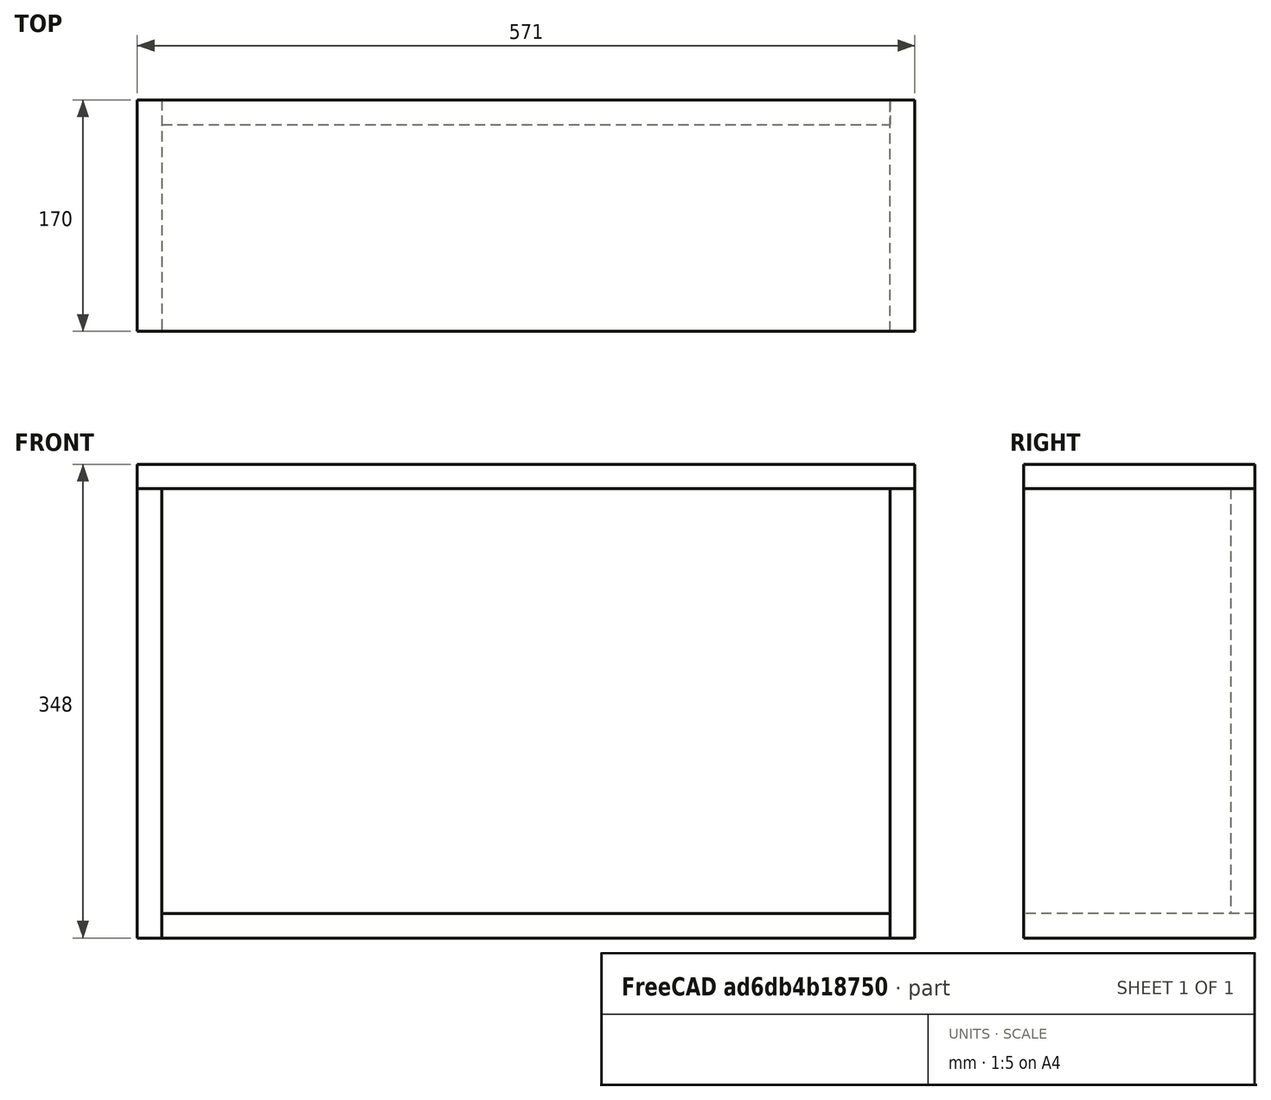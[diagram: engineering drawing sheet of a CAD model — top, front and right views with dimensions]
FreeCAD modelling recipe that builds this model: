
FCSTD DOCUMENT  (FreeCAD 0.17R13541 (Git))
Label: Case_2018-12-29
License: All rights reserved
LicenseURL: http://en.wikipedia.org/wiki/All_rights_reserved
objects: TechDraw::DrawViewDimension×10, Sketcher::SketchObject×5, PartDesign::Pad×5, PartDesign::Body×5, PartDesign::ShapeBinder×5, TechDraw::DrawViewPart×5, TechDraw::DrawSVGTemplate×1, TechDraw::DrawPage×1
note: 25 computed .brp shape members not serialized (recipe doc carries the construction recipe); baked Part::Feature solids carry a one-line shape summary decoded from their .brp

FEATURE [Sketcher::SketchObject] Sketch002
  MapMode = 5
  Placement = pos=(0,0,0) rot=(0.57735,0.57735,0.57735;2.0944rad)
  Support = -> [YZ_Plane002]
  sketch-geometry (4):
    g0: LineSegment StartX=-170 StartY=330 StartZ=0 EndX=0 EndY=330 EndZ=0
    g1: LineSegment StartX=0 StartY=330 StartZ=0 EndX=0 EndY=0 EndZ=0
    g2: LineSegment StartX=0 StartY=0 StartZ=0 EndX=-170 EndY=0 EndZ=0
    g3: LineSegment StartX=-170 StartY=0 StartZ=0 EndX=-170 EndY=330 EndZ=0
  constraints (11):
    c: Coincident(g0,g1)
    c: Coincident(g1,g2)
    c: Coincident(g2,g3)
    c: Coincident(g3,g0)
    c: Horizontal(g0)
    c: Horizontal(g2)
    c: Vertical(g1)
    c: Vertical(g3)
    c: DistanceX(g2,g2) = 170
    c: DistanceY(g3,g3) = 330
    c: Coincident(g-1,g1)
FEATURE [PartDesign::Pad] Pad002
  Length = 18
  Length2 = 100
  Placement = pos=(0,0,0) rot=(0.57735,0.57735,0.57735;2.0944rad)
  Profile = -> Sketch002
  Reversed = true
  Type = 0
FEATURE [PartDesign::Body] Body002  label="RightPlate"
  Group = -> [Sketch002,Pad002]
  Origin = -> Origin002
  Tip = -> Pad002
FEATURE [PartDesign::ShapeBinder] ShapeBinder
  Placement = pos=(-18,0,0) rot=(0,0,1;0rad)
  Support = -> [Pad002]
FEATURE [Sketcher::SketchObject] Sketch001
  ExternalGeometry = -> [ShapeBinder]
  MapMode = 5
  Support = -> [XY_Plane001]
  sketch-geometry (4):
    g0: LineSegment StartX=-553 StartY=0 StartZ=0 EndX=-18 EndY=0 EndZ=0
    g1: LineSegment StartX=-18 StartY=0 StartZ=0 EndX=-18 EndY=-170 EndZ=0
    g2: LineSegment StartX=-18 StartY=-170 StartZ=0 EndX=-553 EndY=-170 EndZ=0
    g3: LineSegment StartX=-553 StartY=-170 StartZ=0 EndX=-553 EndY=0 EndZ=0
  constraints (11):
    c: Coincident(g0,g1)
    c: Coincident(g1,g2)
    c: Coincident(g2,g3)
    c: Coincident(g3,g0)
    c: Horizontal(g0)
    c: Horizontal(g2)
    c: Vertical(g1)
    c: Vertical(g3)
    c: DistanceY(g1,g1) = 170
    c: DistanceX(g0,g0) = 535
    c: Coincident(g0,g-3)
FEATURE [PartDesign::Pad] Pad001
  Length = 18
  Length2 = 100
  Profile = -> Sketch001
  Type = 0
FEATURE [PartDesign::Body] Body001  label="BottomPlate"
  Group = -> [Sketch001,Pad001,ShapeBinder]
  Origin = -> Origin001
  Tip = -> Pad001
FEATURE [PartDesign::ShapeBinder] ShapeBinder001
  Placement = pos=(0,0,18) rot=(0,0,1;0rad)
  Support = -> [Pad001]
FEATURE [Sketcher::SketchObject] Sketch
  ExternalGeometry = -> [ShapeBinder001]
  MapMode = 5
  Placement = pos=(0,0,0) rot=(1,0,0;1.5708rad)
  Support = -> [XZ_Plane]
  sketch-geometry (4):
    g0: LineSegment StartX=-553 StartY=330 StartZ=0 EndX=-18 EndY=330 EndZ=0
    g1: LineSegment StartX=-18 StartY=330 StartZ=0 EndX=-18 EndY=18 EndZ=0
    g2: LineSegment StartX=-18 StartY=18 StartZ=0 EndX=-553 EndY=18 EndZ=0
    g3: LineSegment StartX=-553 StartY=18 StartZ=0 EndX=-553 EndY=330 EndZ=0
  constraints (11):
    c: Coincident(g0,g1)
    c: Coincident(g1,g2)
    c: Coincident(g2,g3)
    c: Coincident(g3,g0)
    c: Horizontal(g0)
    c: Horizontal(g2)
    c: Vertical(g1)
    c: Vertical(g3)
    c: DistanceX(g2,g2) = 535
    c: DistanceY(g1,g1) = 312
    c: Coincident(g1,g-3)
FEATURE [PartDesign::Pad] Pad
  Length = 18
  Length2 = 100
  Placement = pos=(0,0,0) rot=(1,0,0;1.5708rad)
  Profile = -> Sketch
  Type = 0
FEATURE [PartDesign::Body] Body  label="BackPlate"
  Group = -> [Sketch,Pad,ShapeBinder001]
  Origin = -> Origin
  Tip = -> Pad
FEATURE [PartDesign::ShapeBinder] ShapeBinder002
  Support = -> [Pad001]
FEATURE [Sketcher::SketchObject] Sketch003
  MapMode = 5
  Placement = pos=(-553,0,0) rot=(0.57735,-0.57735,-0.57735;2.0944rad)
  Support = -> [ShapeBinder002]
  sketch-geometry (4):
    g0: LineSegment StartX=0 StartY=330 StartZ=0 EndX=170 EndY=330 EndZ=0
    g1: LineSegment StartX=170 StartY=330 StartZ=0 EndX=170 EndY=0 EndZ=0
    g2: LineSegment StartX=170 StartY=0 StartZ=0 EndX=0 EndY=0 EndZ=0
    g3: LineSegment StartX=0 StartY=0 StartZ=0 EndX=0 EndY=330 EndZ=0
  constraints (11):
    c: Coincident(g0,g1)
    c: Coincident(g1,g2)
    c: Coincident(g2,g3)
    c: Coincident(g3,g0)
    c: Horizontal(g0)
    c: Horizontal(g2)
    c: Vertical(g1)
    c: Vertical(g3)
    c: DistanceX(g2,g2) = 170
    c: DistanceY(g3,g3) = 330
    c: Coincident(g-1,g2)
FEATURE [PartDesign::Pad] Pad003
  Length = 18
  Length2 = 100
  Profile = -> Sketch003
  Type = 0
FEATURE [PartDesign::Body] Body003  label="LeftPlate"
  Group = -> [ShapeBinder002,Sketch003,Pad003]
  Origin = -> Origin003
  Tip = -> Pad003
FEATURE [PartDesign::ShapeBinder] ShapeBinder003
  Placement = pos=(0,0,0) rot=(0.57735,0.57735,0.57735;2.0944rad)
  Support = -> [Pad002]
FEATURE [PartDesign::ShapeBinder] ShapeBinder004
  Support = -> [Pad003]
FEATURE [Sketcher::SketchObject] Sketch004
  ExternalGeometry = -> [ShapeBinder004]
  MapMode = 5
  Placement = pos=(0,0,330) rot=(0,0,-1;1.5708rad)
  Support = -> [ShapeBinder003]
  sketch-geometry (4):
    g0: LineSegment StartX=0 StartY=0 StartZ=0 EndX=170 EndY=0 EndZ=0
    g1: LineSegment StartX=170 StartY=0 StartZ=0 EndX=170 EndY=-571 EndZ=0
    g2: LineSegment StartX=170 StartY=-571 StartZ=0 EndX=0 EndY=-571 EndZ=0
    g3: LineSegment StartX=0 StartY=-571 StartZ=0 EndX=0 EndY=0 EndZ=0
  constraints (11):
    c: Coincident(g0,g1)
    c: Coincident(g1,g2)
    c: Coincident(g2,g3)
    c: Coincident(g3,g0)
    c: Horizontal(g0)
    c: Horizontal(g2)
    c: Vertical(g1)
    c: Vertical(g3)
    c: DistanceX(g0,g0) = 170
    c: Coincident(g0,g-1)
    c: Coincident(g2,g-3)
FEATURE [PartDesign::Pad] Pad004
  Length = 18
  Length2 = 100
  Placement = pos=(0,0,0) rot=(0.57735,0.57735,0.57735;2.0944rad)
  Profile = -> Sketch004
  Type = 0
FEATURE [PartDesign::Body] Body004  label="TopPlate"
  Group = -> [ShapeBinder003,Sketch004,ShapeBinder004,Pad004]
  Origin = -> Origin004
  Tip = -> Pad004
FEATURE [TechDraw::DrawSVGTemplate] Template
  EditableTexts = Designed_by_Name=Oliver Walczak; Drawing_number=1; FC-Date=29.12.2018; FC-SC=0,2; FC-SH=1; FC-Title=Eurorack; Subtitle=Topcase; Weight=-
  Height = 210
  Orientation = 1
  Width = 297
FEATURE [TechDraw::DrawViewPart] View
  Caption = BackPlate
  CoarseView = false
  Direction = (0,1,0)
  Focus = 100
  HardHidden = false
  IsoCount = 0
  IsoHidden = false
  IsoVisible = false
  LockPosition = false
  Perspective = false
  Rotation = 0
  Scale = 0.2
  ScaleType = 0
  SeamHidden = false
  SeamVisible = false
  SmoothHidden = false
  SmoothVisible = false
  Source = -> [Body]
  X = 86.011
  Y = 155.517
FEATURE [TechDraw::DrawViewDimension] Dimension
  FormatSpec = %.2f
  LockPosition = false
  MeasureType = 1
  References2D = -> [View]
  Rotation = 0
  Scale = 0.2
  ScaleType = 0
  Type = 1
  X = -2.04403
  Y = 39.1286
FEATURE [TechDraw::DrawViewDimension] Dimension001
  FormatSpec = %.2f
  LockPosition = false
  MeasureType = 1
  References2D = -> [View]
  Rotation = 0
  Scale = 0.2
  ScaleType = 0
  Type = 2
  X = -63.365
  Y = -1.46002
FEATURE [TechDraw::DrawViewPart] View001
  Caption = BottomPlate
  CoarseView = false
  Direction = (0,0,1)
  Focus = 100
  HardHidden = false
  IsoCount = 0
  IsoHidden = false
  IsoVisible = false
  LockPosition = false
  Perspective = false
  Rotation = 0
  Scale = 0.2
  ScaleType = 0
  SeamHidden = false
  SeamVisible = false
  SmoothHidden = false
  SmoothVisible = false
  Source = -> [Body001]
  X = 217.121
  Y = 98.2839
FEATURE [TechDraw::DrawViewDimension] Dimension002
  FormatSpec = %.2f
  LockPosition = false
  MeasureType = 1
  References2D = -> [View001]
  Rotation = 0
  Scale = 0.2
  ScaleType = 0
  Type = 1
  X = -0.876014
  Y = 25.1124
FEATURE [TechDraw::DrawViewDimension] Dimension003
  FormatSpec = %.2f
  LockPosition = false
  MeasureType = 1
  References2D = -> [View001]
  Rotation = 0
  Scale = 0.2
  ScaleType = 0
  Type = 2
  X = -62.197
  Y = 0.292005
FEATURE [TechDraw::DrawViewPart] View002
  Caption = TopPlate
  CoarseView = false
  Direction = (0,0,1)
  Focus = 100
  HardHidden = false
  IsoCount = 0
  IsoHidden = false
  IsoVisible = false
  LockPosition = false
  Perspective = false
  Rotation = 0
  Scale = 0.2
  ScaleType = 0
  SeamHidden = false
  SeamVisible = false
  SmoothHidden = false
  SmoothVisible = false
  Source = -> [Body004]
  X = 215.953
  Y = 168.073
FEATURE [TechDraw::DrawViewDimension] Dimension004
  FormatSpec = %.2f
  LockPosition = false
  MeasureType = 1
  References2D = -> [View002]
  Rotation = 0
  Scale = 0.2
  ScaleType = 0
  Type = 1
  X = -1.75203
  Y = 24.5284
FEATURE [TechDraw::DrawViewDimension] Dimension005
  FormatSpec = %.2f
  LockPosition = false
  MeasureType = 1
  References2D = -> [View002]
  Rotation = 0
  Scale = 0.2
  ScaleType = 0
  Type = 2
  X = -64.825
  Y = -1.16802
FEATURE [TechDraw::DrawViewPart] View003
  Caption = LeftPlate
  CoarseView = false
  Direction = (1,0,0)
  Focus = 100
  HardHidden = false
  IsoCount = 0
  IsoHidden = false
  IsoVisible = false
  LockPosition = false
  Perspective = false
  Rotation = 0
  Scale = 0.2
  ScaleType = 0
  SeamHidden = false
  SeamVisible = false
  SmoothHidden = false
  SmoothVisible = false
  Source = -> [Body003]
  X = 51.8465
  Y = 66.7474
FEATURE [TechDraw::DrawViewDimension] Dimension006
  FormatSpec = %.2f
  LockPosition = false
  MeasureType = 1
  References2D = -> [View003]
  Rotation = 0
  Scale = 0.2
  ScaleType = 0
  Type = 1
  X = 1.16802
  Y = 39.7126
FEATURE [TechDraw::DrawViewDimension] Dimension007
  FormatSpec = %.2f
  LockPosition = false
  MeasureType = 1
  References2D = -> [View003]
  Rotation = 0
  Scale = 0.2
  ScaleType = 0
  Type = 2
  X = -24.2364
  Y = -2.62804
FEATURE [TechDraw::DrawViewPart] View004
  Caption = RightPlate
  CoarseView = false
  Direction = (1,0,0)
  Focus = 100
  HardHidden = false
  IsoCount = 0
  IsoHidden = false
  IsoVisible = false
  LockPosition = false
  Perspective = false
  Rotation = 0
  Scale = 0.2
  ScaleType = 0
  SeamHidden = false
  SeamVisible = false
  SmoothHidden = false
  SmoothVisible = false
  Source = -> [Body002]
  X = 107.619
  Y = 66.7474
FEATURE [TechDraw::DrawViewDimension] Dimension008
  FormatSpec = %.2f
  LockPosition = false
  MeasureType = 1
  References2D = -> [View004]
  Rotation = 0
  Scale = 0.2
  ScaleType = 0
  Type = 1
  X = 0.876014
  Y = 39.4206
FEATURE [TechDraw::DrawViewDimension] Dimension009
  FormatSpec = %.2f
  LockPosition = false
  MeasureType = 1
  References2D = -> [View004]
  Rotation = 0
  Scale = 0.2
  ScaleType = 0
  Type = 2
  X = -23.6524
  Y = -1.75203
FEATURE [TechDraw::DrawPage] Page
  KeepUpdated = true
  ProjectionType = 0
  Scale = 0.2
  Template = -> Template
  Views = -> [View,Dimension,Dimension001,View001,Dimension002,Dimension003,View002,Dimension004,Dimension005,View003,Dimension006,Dimension007,View004,Dimension008,Dimension009]
  expr: Scale = 0.20000000000000001
